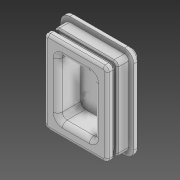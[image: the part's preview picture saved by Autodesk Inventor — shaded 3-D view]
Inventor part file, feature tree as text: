
AUTODESK INVENTOR PART (.ipt)
format: ipt  version: 2021 (Build 250183000, 183)  size: 450,560 bytes
history: native  units: mm
features: extrude x11, sketch x10, projected_geometry x5, chamfer x3, fillet x3
ambient origin geometry x8: Origin, YZ Plane, XZ Plane, XY Plane, X Axis, Y Axis, Z Axis, Center Point
bodies: Body1 (feature_tree)
feature tree (32):
  sketch  "Boceto1"  dims[d17=27.75mm d18=36.38mm]
  extrude  "Extrusión5"  Depth=36.38mm
  extrude  "Extrusión6"  Depth=2.0mm
  chamfer  "Chaflán2"  Distance=3.0mm
  extrude  "Extrusión7"  Depth=1.5mm TaperAngle=45.0deg
  extrude  "Extrusión8"  Depth=5.0mm
  extrude  "Extrusión9"  Depth=5.0mm
  chamfer  "Chaflán3"  Distance=5.0mm
  chamfer  "Chaflán4"  Distance=1.2mm
  extrude  "Extrusión11"  Depth=0.8mm TaperAngle=45.0deg
  fillet  "Empalme4"  Radius=10.0mm
  extrude  "Extrusión12"  Depth=2.0mm
  extrude  "Extrusión13"  Depth=10.0mm TaperAngle=0.0deg
  extrude  "Extrusión14"  Depth=2.0mm
  extrude  "Extrusión15"  Depth=2.0mm TaperAngle=0.0deg
  extrude  "Extrusión16"  Depth=2.0mm
  fillet  "Empalme7"  Radius=10.0mm
  fillet  "Empalme8"  Radius=10.0mm
  sketch  "Boceto4"  dims[d19=2.0mm d20=2.0mm d21=3.0mm d22=0.0mm]
  sketch  "Boceto5"  dims[d23=8.0mm d24=0.0mm d28=1.5mm d29=2.0mm d30=45.0deg]
  projected_geometry  "Contorno proyectado2"
  sketch  "Boceto6"  dims[d31=5.0mm d32=5.0mm]
  projected_geometry  "Contorno proyectado3"
  sketch  "Boceto8"  dims[d33=5.0mm d34=5.0mm d35=5.0mm d36=0.0mm]
  sketch  "Boceto9"  dims[d37=1.4mm]
  projected_geometry  "Contorno proyectado5"
  sketch  "Boceto10"  dims[d38=2.0mm d39=1.2mm d40=0.0mm]
  sketch  "Boceto11"  dims[d41=3.0mm d42=0.0mm d43=0.8mm d44=2.0mm d45=45.0deg]
  sketch  "Boceto12"  dims[d46=0.8mm d47=2.0mm d48=45.0deg d55=10.0mm d56=0.0mm]
  projected_geometry  "Contorno proyectado7"
  projected_geometry  "Contorno proyectado8"
  sketch  "Boceto13"  dims[d57=1.5mm d58=4.5mm d59=10.0mm d60=0.0mm d63=12.0mm d64=0.35mm d65=0.0mm d66=0.18mm d67=10.0mm d68=0.0mm d69=10.0mm d70=0.0mm d71=10.0mm d72=0.0mm d73=2.0mm d74=2.0mm]
